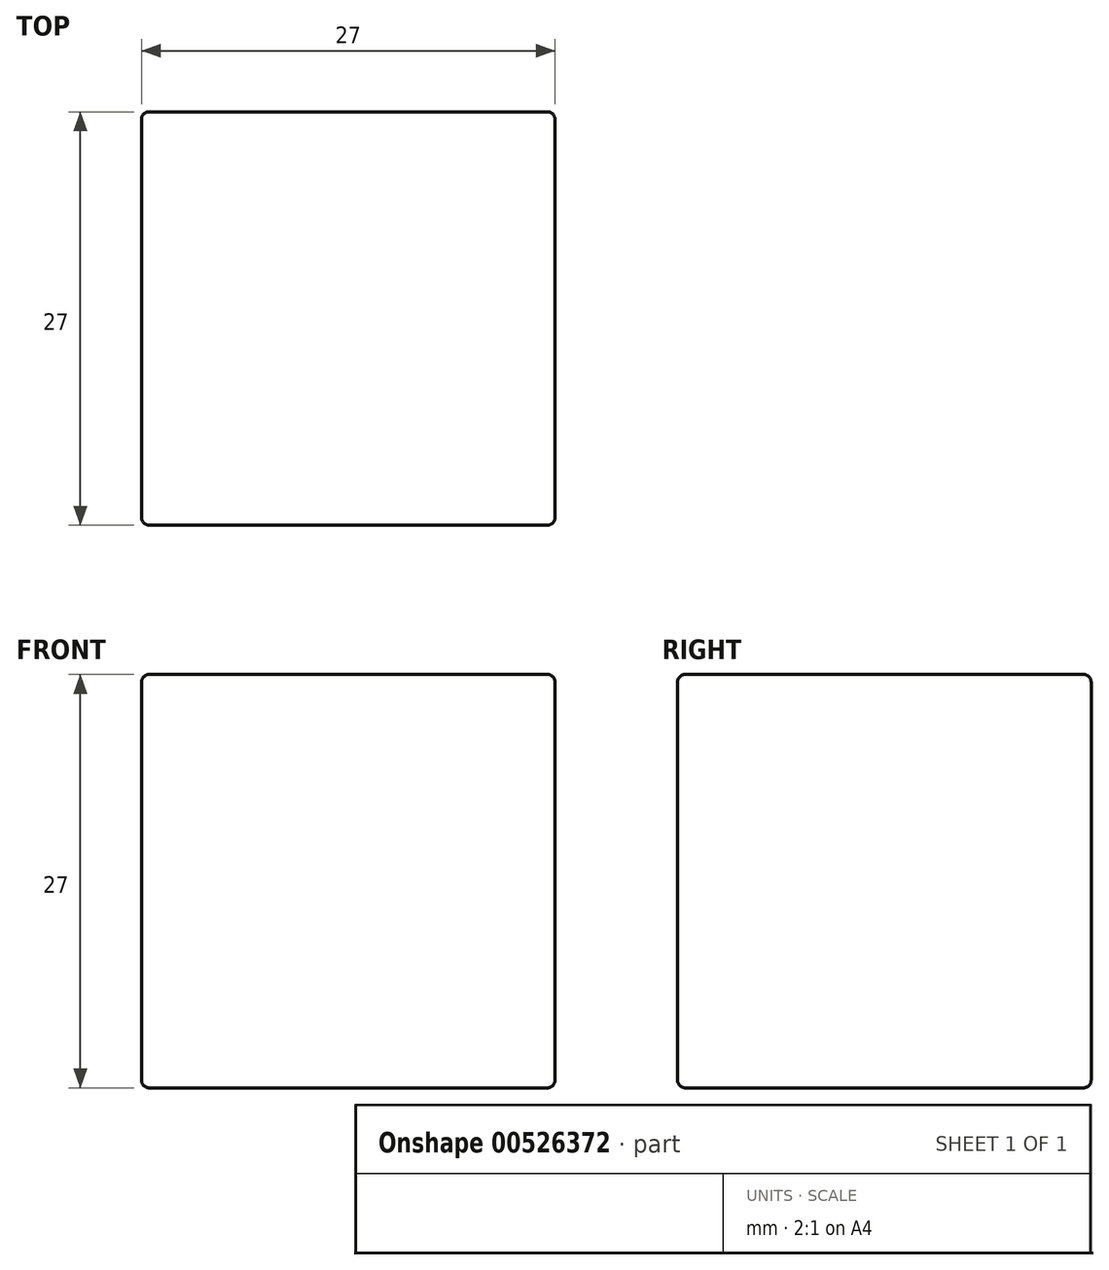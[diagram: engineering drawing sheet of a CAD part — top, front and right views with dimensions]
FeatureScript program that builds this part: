
annotation { "Feature Type Name" : "Feature", "Feature Type Description" : "" }
export const myFeature = defineFeature(function(context is Context, id is Id, definition is map)
    precondition{}
    {
        {
            var Q0;
            Q0=qCreatedBy(makeId("Top.planeOp"),FACE);
            var sketch = newSketch(context, id + "F0", { "sketchPlane" : qUnion([Q0])});
            skLineSegment(sketch, "E0.bottom", {"start": v(13.5, -13.5) * mm, "end": v(-13.5, -13.5) * mm});
            skLineSegment(sketch, "E0.top", {"start": v(13.5, 13.5) * mm, "end": v(-13.5, 13.5) * mm});
            skLineSegment(sketch, "E0.left", {"start": v(13.5, -13.5) * mm, "end": v(13.5, 13.5) * mm});
            skLineSegment(sketch, "E0.right", {"start": v(-13.5, -13.5) * mm, "end": v(-13.5, 13.5) * mm});
            skPoint(sketch, "E0.middle", {"position": v(0, 0) * mm});
            skSolve(sketch);
        }
        {
            var Q0;
            Q0=makeQuery(id+"F0.imprint","IMPRINT",FACE,{"disambiguationData":[TD([[makeQuery(id+"F0.imprint","IMPRINT",EDGE,{"derivedFrom":sQuery(id+"F0.wireOp",EDGE,"E0.bottom")}),-1.0]])]});
            extrude(context, id + "F1", {"entities" : qUnion([Q0]), "depth" : 27 * mm, "offsetDistance" : 25 * mm});
        }
        {
            var Q0;
            Q0=makeQuery(id+"F1.opExtrude","CAP_EDGE",EDGE,{"disambiguationData":[OSD([sQuery(id+"F0.wireOp",EDGE,"E0.left")])],"isStart":false});
            var Q1;
            Q1=makeQuery(id+"F1.opExtrude","CAP_EDGE",EDGE,{"disambiguationData":[OSD([sQuery(id+"F0.wireOp",EDGE,"E0.bottom")])],"isStart":false});
            var Q2;
            Q2=makeQuery(id+"F1.opExtrude","CAP_EDGE",EDGE,{"disambiguationData":[OSD([sQuery(id+"F0.wireOp",EDGE,"E0.right")])],"isStart":false});
            var Q3;
            Q3=makeQuery(id+"F1.opExtrude","CAP_EDGE",EDGE,{"disambiguationData":[OSD([sQuery(id+"F0.wireOp",EDGE,"E0.top")])],"isStart":false});
            var Q4;
            Q4=makeQuery(id+"F1.opExtrude","SWEPT_EDGE",EDGE,{"disambiguationData":[OSD([sQuery(id+"F0.wireOp",EDGE,"E0.top"),sQuery(id+"F0.wireOp",EDGE,"E0.left")])]});
            var Q5;
            Q5=makeQuery(id+"F1.opExtrude","SWEPT_EDGE",EDGE,{"disambiguationData":[OSD([sQuery(id+"F0.wireOp",EDGE,"E0.bottom"),sQuery(id+"F0.wireOp",EDGE,"E0.left")])]});
            var Q6;
            Q6=makeQuery(id+"F1.opExtrude","SWEPT_EDGE",EDGE,{"disambiguationData":[OSD([sQuery(id+"F0.wireOp",EDGE,"E0.bottom"),sQuery(id+"F0.wireOp",EDGE,"E0.right")])]});
            var Q7;
            Q7=makeQuery(id+"F1.opExtrude","SWEPT_FACE",FACE,{"disambiguationData":[OSD([sQuery(id+"F0.wireOp",EDGE,"E0.bottom")])]});
            var Q8;
            Q8=makeQuery(id+"F1.opExtrude","CAP_EDGE",EDGE,{"disambiguationData":[OSD([sQuery(id+"F0.wireOp",EDGE,"E0.left")])],"isStart":true});
            var Q9;
            Q9=makeQuery(id+"F1.opExtrude","CAP_EDGE",EDGE,{"disambiguationData":[OSD([sQuery(id+"F0.wireOp",EDGE,"E0.top")])],"isStart":true});
            var Q10;
            Q10=makeQuery(id+"F1.opExtrude","SWEPT_EDGE",EDGE,{"disambiguationData":[OSD([sQuery(id+"F0.wireOp",EDGE,"E0.top"),sQuery(id+"F0.wireOp",EDGE,"E0.right")])]});
            var Q11;
            Q11=makeQuery(id+"F1.opExtrude","CAP_EDGE",EDGE,{"disambiguationData":[OSD([sQuery(id+"F0.wireOp",EDGE,"E0.right")])],"isStart":true});
            fillet(context, id + "F2", {"entities" : qUnion([Q0, Q1, Q2, Q3, Q4, Q5, Q6, Q7, Q8, Q9, Q10, Q11]), "radius" : 0.5 * mm, "tangentPropagation" : true, "allowEdgeOverflow" : false});
        }
    });
